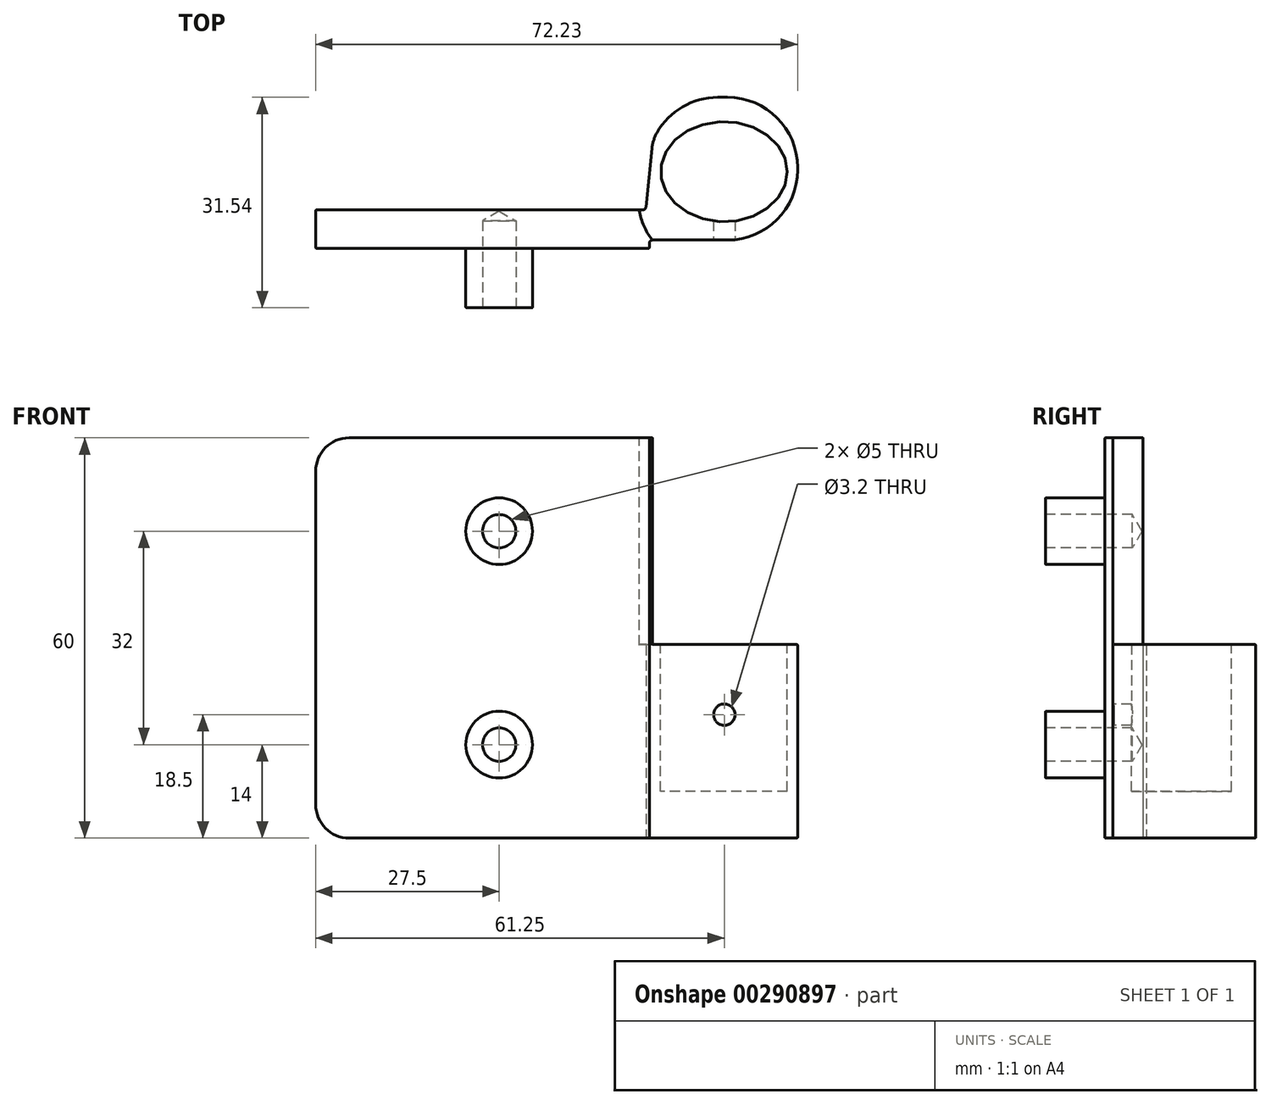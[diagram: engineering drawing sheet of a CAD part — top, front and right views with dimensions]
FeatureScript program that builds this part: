
annotation { "Feature Type Name" : "Feature", "Feature Type Description" : "" }
export const myFeature = defineFeature(function(context is Context, id is Id, definition is map)
    precondition{}
    {
        {
            var Q0;
            Q0=qCreatedBy(makeId("Front.planeOp"),FACE);
            var sketch = newSketch(context, id + "F0", { "sketchPlane" : qUnion([Q0])});
            skLineSegment(sketch, "E0", {"start": v(0, 0) * mm, "end": v(-48.5, 0) * mm});
            skLineSegment(sketch, "E1", {"start": v(-48.5, 0) * mm, "end": v(-48.5, -5.75) * mm});
            skLineSegment(sketch, "E2", {"start": v(-48.5, -5.75) * mm, "end": v(1.5, -5.75) * mm});
            skLineSegment(sketch, "E3", {"start": v(1.5, -5.75) * mm, "end": v(1.5, -5) * mm});
            skLineSegment(sketch, "E4", {"start": v(2, -4.5) * mm, "end": v(3.23, -4.5) * mm});
            skLineSegment(sketch, "E5", {"start": v(3.23, -4.5) * mm, "end": v(13.23, -4.5) * mm});
            skLineSegment(sketch, "E6", {"start": v(23.73, 6) * mm, "end": v(23.73, 6.4) * mm});
            skLineSegment(sketch, "E7", {"start": v(13.23, 16.9) * mm, "end": v(11.78, 16.9) * mm});
            skLineSegment(sketch, "E8", {"start": v(0.5, 0) * mm, "end": v(0, 0) * mm});
            skArc(sketch, "E9.filletArc", {"start": v(13.23, -4.5) * mm, "mid": v(20.66, -1.43) * mm, "end": v(23.73, 6) * mm});
            skArc(sketch, "E10.filletArc", {"start": v(23.73, 6.4) * mm, "mid": v(20.66, 13.82) * mm, "end": v(13.23, 16.9) * mm});
            skArc(sketch, "E11.filletArc", {"start": v(11.78, 16.9) * mm, "mid": v(6.5, 15.47) * mm, "end": v(2.65, 11.6) * mm});
            skArc(sketch, "E12.filletArc", {"start": v(0.5, 0) * mm, "mid": v(0.85, 0.15) * mm, "end": v(1, 0.5) * mm});
            skPoint(sketch, "E13.visualSharp", {"position": v(1.5, -4.5) * mm});
            skArc(sketch, "E13.filletArc", {"start": v(2, -4.5) * mm, "mid": v(1.65, -4.66) * mm, "end": v(1.5, -5) * mm});
            skLineSegment(sketch, "E14", {"start": v(1, 0.5) * mm, "end": v(1.9, 9.23) * mm});
            skPoint(sketch, "E15.visualSharp", {"position": v(2, 10.22) * mm});
            skArc(sketch, "E15.filletArc", {"start": v(2.65, 11.6) * mm, "mid": v(2.15, 10.45) * mm, "end": v(1.9, 9.23) * mm});
            skSolve(sketch);
        }
        {
            var Q0;
            Q0=makeQuery(id+"F0.imprint","IMPRINT",FACE,{"disambiguationData":[TD([[makeQuery(id+"F0.imprint","IMPRINT",EDGE,{"derivedFrom":sQuery(id+"F0.wireOp",EDGE,"E0")}),1.0]])]});
            extrude(context, id + "F1", {"entities" : qUnion([Q0]), "depth" : 60 * mm});
        }
        {
            var Q0;
            Q0=makeQuery(id+"F1.opExtrude","CAP_EDGE",EDGE,{"disambiguationData":[OSD([sQuery(id+"F0.wireOp",EDGE,"E1")])],"isStart":false});
            var Q1;
            Q1=makeQuery(id+"F1.opExtrude","CAP_EDGE",EDGE,{"disambiguationData":[OSD([sQuery(id+"F0.wireOp",EDGE,"E1")])],"isStart":true});
            fillet(context, id + "F2", {"entities" : qUnion([Q0, Q1]), "radius" : 5 * mm, "tangentPropagation" : true, "allowEdgeOverflow" : false});
        }
        {
            var Q0;
            Q0=makeQuery(id+"F1.opExtrude","SWEPT_FACE",FACE,{"disambiguationData":[OSD([sQuery(id+"F0.wireOp",EDGE,"E4"),sQuery(id+"F0.wireOp",EDGE,"E5")])]});
            var sketch = newSketch(context, id + "F3", { "sketchPlane" : qUnion([Q0])});
            skLineSegment(sketch, "E16.bottom", {"start": v(2, 60) * mm, "end": v(31.94, 60) * mm});
            skLineSegment(sketch, "E16.top", {"start": v(2, 29) * mm, "end": v(31.94, 29) * mm});
            skLineSegment(sketch, "E16.left", {"start": v(2, 60) * mm, "end": v(2, 29) * mm});
            skLineSegment(sketch, "E16.right", {"start": v(31.94, 60) * mm, "end": v(31.94, 29) * mm});
            skSolve(sketch);
        }
        {
            var Q0;
            Q0=qSketchRegion(id+"F3",true);
            extrude(context, id + "F4", {"entities" : qUnion([Q0]), "operationType" : NewBodyOperationType.REMOVE, "endBound" : BoundingType.THROUGH_ALL, "oppositeDirection" : true, "depth" : 25 * mm});
        }
        {
            var Q0;
            Q0=makeQuery(id+"F1.opExtrude","CAP_FACE",FACE,{"disambiguationData":[OSD([sQuery(id+"F0.wireOp",EDGE,"E0"),sQuery(id+"F0.wireOp",EDGE,"E1"),sQuery(id+"F0.wireOp",EDGE,"E2"),sQuery(id+"F0.wireOp",EDGE,"E3"),sQuery(id+"F0.wireOp",EDGE,"E4"),sQuery(id+"F0.wireOp",EDGE,"E5"),sQuery(id+"F0.wireOp",EDGE,"E6"),sQuery(id+"F0.wireOp",EDGE,"E7"),sQuery(id+"F0.wireOp",EDGE,"GG9Xp7Lx-0V8L-KjhP-dehT-RjXL1Wiv3JEy"),sQuery(id+"F0.wireOp",EDGE,"E8"),sQuery(id+"F0.wireOp",EDGE,"E9.filletArc"),sQuery(id+"F0.wireOp",EDGE,"E10.filletArc"),sQuery(id+"F0.wireOp",EDGE,"E11.filletArc"),sQuery(id+"F0.wireOp",EDGE,"E12.filletArc"),sQuery(id+"F0.wireOp",EDGE,"E13.filletArc")])],"isStart":false});
            var sketch = newSketch(context, id + "F5", { "sketchPlane" : qUnion([Q0])});
            skArc(sketch, "E17", {"start": v(0, 0) * mm, "mid": v(0.68, -2.4) * mm, "end": v(2, -4.5) * mm});
            skLineSegment(sketch, "E18", {"start": v(2, -4.5) * mm, "end": v(4.6, -0.03) * mm});
            skLineSegment(sketch, "E19", {"start": v(4.6, -0.03) * mm, "end": v(2.71, 13.2) * mm});
            skLineSegment(sketch, "E20", {"start": v(2.71, 13.2) * mm, "end": v(-1.4, 7.63) * mm});
            skLineSegment(sketch, "E21", {"start": v(0, 0) * mm, "end": v(-1.4, 7.63) * mm});
            skSolve(sketch);
        }
        {
            var Q0;
            Q0=qSketchRegion(id+"F5",true);
            extrude(context, id + "F6", {"entities" : qUnion([Q0]), "operationType" : NewBodyOperationType.REMOVE, "oppositeDirection" : true, "depth" : 31 * mm});
        }
        {
            var Q0;
            Q0=makeQuery(id+"F1.opExtrude","SWEPT_BODY",BODY,{"disambiguationData":[OSD([sQuery(id+"F0.wireOp",EDGE,"E0"),sQuery(id+"F0.wireOp",EDGE,"E1"),sQuery(id+"F0.wireOp",EDGE,"E2"),sQuery(id+"F0.wireOp",EDGE,"E3"),sQuery(id+"F0.wireOp",EDGE,"E4"),sQuery(id+"F0.wireOp",EDGE,"E5"),sQuery(id+"F0.wireOp",EDGE,"E6"),sQuery(id+"F0.wireOp",EDGE,"E7"),sQuery(id+"F0.wireOp",EDGE,"GG9Xp7Lx-0V8L-KjhP-dehT-RjXL1Wiv3JEy"),sQuery(id+"F0.wireOp",EDGE,"E8"),sQuery(id+"F0.wireOp",EDGE,"E9.filletArc"),sQuery(id+"F0.wireOp",EDGE,"E10.filletArc"),sQuery(id+"F0.wireOp",EDGE,"E11.filletArc"),sQuery(id+"F0.wireOp",EDGE,"E12.filletArc"),sQuery(id+"F0.wireOp",EDGE,"E13.filletArc")])]});
            var Q1;
            Q1=makeQuery(id+"F1.opExtrude","CAP_EDGE",EDGE,{"disambiguationData":[OSD([sQuery(id+"F0.wireOp",EDGE,"E0"),sQuery(id+"F0.wireOp",EDGE,"E8")])],"isStart":true});
            transform(context, id + "F7", {"entities" : qUnion([Q0]), "transformType" : TransformType.ROTATION, "transformAxis" : qUnion([Q1]), "angle" : 90 * degree, "makeCopy" : false});
        }
        {
            var Q0;
            Q0=makeQuery(id+"F1.opExtrude","SWEPT_FACE",FACE,{"disambiguationData":[OSD([sQuery(id+"F0.wireOp",EDGE,"E2")])]});
            var sketch = newSketch(context, id + "F8", { "sketchPlane" : qUnion([Q0])});
            skCircle(sketch, "E22", {"center": v(-21, 46) * mm, "radius": 5 * mm});
            skCircle(sketch, "E23", {"center": v(-21, 14) * mm, "radius": 5 * mm});
            skSolve(sketch);
        }
        {
            var Q0;
            Q0=qSketchRegion(id+"F8",true);
            extrude(context, id + "F9", {"entities" : qUnion([Q0]), "operationType" : NewBodyOperationType.ADD, "depth" : 8.9 * mm});
        }
        {
            var Q0;
            Q0=makeQuery(id+"F9.opExtrude","CAP_FACE",FACE,{"disambiguationData":[OSD([sQuery(id+"F8.wireOp",EDGE,"E22")])],"isStart":false});
            var sketch = newSketch(context, id + "F10", { "sketchPlane" : qUnion([Q0])});
            skCircle(sketch, "E24", {"center": v(-21, 46) * mm, "radius": 2.5 * mm});
            skSolve(sketch);
        }
        {
            var Q0;
            Q0=makeQuery(id+"F9.opExtrude","CAP_FACE",FACE,{"disambiguationData":[OSD([sQuery(id+"F8.wireOp",EDGE,"E23")])],"isStart":false});
            var sketch = newSketch(context, id + "F11", { "sketchPlane" : qUnion([Q0])});
            skCircle(sketch, "E25", {"center": v(-21, 14) * mm, "radius": 2.5 * mm});
            skSolve(sketch);
        }
        {
            var Q0;
            Q0=sQuery(id+"F10.wireOp",VERTEX,"E24.center");
            var Q1;
            Q1=makeQuery(id+"F1.opExtrude","SWEPT_BODY",BODY,{"disambiguationData":[OSD([sQuery(id+"F0.wireOp",EDGE,"E0"),sQuery(id+"F0.wireOp",EDGE,"E1"),sQuery(id+"F0.wireOp",EDGE,"E2"),sQuery(id+"F0.wireOp",EDGE,"E3"),sQuery(id+"F0.wireOp",EDGE,"E4"),sQuery(id+"F0.wireOp",EDGE,"E5"),sQuery(id+"F0.wireOp",EDGE,"E6"),sQuery(id+"F0.wireOp",EDGE,"E7"),sQuery(id+"F0.wireOp",EDGE,"GG9Xp7Lx-0V8L-KjhP-dehT-RjXL1Wiv3JEy"),sQuery(id+"F0.wireOp",EDGE,"E8"),sQuery(id+"F0.wireOp",EDGE,"E9.filletArc"),sQuery(id+"F0.wireOp",EDGE,"E10.filletArc"),sQuery(id+"F0.wireOp",EDGE,"E11.filletArc"),sQuery(id+"F0.wireOp",EDGE,"E12.filletArc"),sQuery(id+"F0.wireOp",EDGE,"E13.filletArc")])]});
            hole(context, id + "F12", {"style" : HoleStyle.SIMPLE, "endStyle" : HoleEndStyle.BLIND, "standardTappedOrClearance" : lookupTablePath({ "standard" : "ISO", "engagement" : "75%", "pitch" : "1 mm", "size" : "M6", "type" : "Tapped" }), "standardBlindInLast" : lookupTablePath({ "standard" : "ISO", "engagement" : "75%", "pitch" : "1 mm", "size" : "M6", "type" : "Tapped" }), "holeDiameter" : 5 * mm, "showTappedDepth" : true, "holeDepth" : 13 * mm, "tappedDepth" : 10 * mm, "tapClearance" : 3, "locations" : qUnion([Q0]), "scope" : qUnion([Q1]), "majorDiameter" : 6 * mm});
        }
        {
            var Q0;
            Q0=sQuery(id+"F11.wireOp",VERTEX,"E25.center");
            var Q1;
            Q1=makeQuery(id+"F1.opExtrude","SWEPT_BODY",BODY,{"disambiguationData":[OSD([sQuery(id+"F0.wireOp",EDGE,"E0"),sQuery(id+"F0.wireOp",EDGE,"E1"),sQuery(id+"F0.wireOp",EDGE,"E2"),sQuery(id+"F0.wireOp",EDGE,"E3"),sQuery(id+"F0.wireOp",EDGE,"E4"),sQuery(id+"F0.wireOp",EDGE,"E5"),sQuery(id+"F0.wireOp",EDGE,"E6"),sQuery(id+"F0.wireOp",EDGE,"E7"),sQuery(id+"F0.wireOp",EDGE,"GG9Xp7Lx-0V8L-KjhP-dehT-RjXL1Wiv3JEy"),sQuery(id+"F0.wireOp",EDGE,"E8"),sQuery(id+"F0.wireOp",EDGE,"E9.filletArc"),sQuery(id+"F0.wireOp",EDGE,"E10.filletArc"),sQuery(id+"F0.wireOp",EDGE,"E11.filletArc"),sQuery(id+"F0.wireOp",EDGE,"E12.filletArc"),sQuery(id+"F0.wireOp",EDGE,"E13.filletArc")])]});
            hole(context, id + "F13", {"style" : HoleStyle.SIMPLE, "endStyle" : HoleEndStyle.BLIND, "standardTappedOrClearance" : lookupTablePath({ "standard" : "ISO", "engagement" : "75%", "pitch" : "1 mm", "size" : "M6", "type" : "Tapped" }), "standardBlindInLast" : lookupTablePath({ "standard" : "ISO", "engagement" : "75%", "pitch" : "1 mm", "size" : "M6", "type" : "Tapped" }), "holeDiameter" : 5 * mm, "showTappedDepth" : true, "holeDepth" : 13 * mm, "tappedDepth" : 10 * mm, "tapClearance" : 3, "locations" : qUnion([Q0]), "scope" : qUnion([Q1]), "majorDiameter" : 6 * mm});
        }
        {
            var Q0;
            Q0=makeQuery(id+"F6.boolean.opBoolean","MERGE",FACE,{"derivedFrom":[makeQuery(id+"F4.boolean.opBoolean","COPY",FACE,{"derivedFrom":makeQuery(id+"F4.opExtrude","SWEPT_FACE",FACE,{"disambiguationData":[OSD([sQuery(id+"F3.wireOp",EDGE,"E16.top")])]})}),makeQuery(id+"F6.opExtrude","CAP_FACE",FACE,{"disambiguationData":[OSD([sQuery(id+"F5.wireOp",EDGE,"E17"),sQuery(id+"F5.wireOp",EDGE,"E18"),sQuery(id+"F5.wireOp",EDGE,"E19"),sQuery(id+"F5.wireOp",EDGE,"E20"),sQuery(id+"F5.wireOp",EDGE,"E21")])],"isStart":false})]});
            var sketch = newSketch(context, id + "F14", { "sketchPlane" : qUnion([Q0])});
            skEllipse(sketch, "E26", {"center": v(12.7, 5.75) * mm, "majorRadius": 9.5 * mm, "minorRadius": 7.5 * mm, "majorAxis": v(1, 0)});
            skSolve(sketch);
        }
        {
            var Q0;
            Q0=qSketchRegion(id+"F14",true);
            extrude(context, id + "F15", {"entities" : qUnion([Q0]), "operationType" : NewBodyOperationType.REMOVE, "oppositeDirection" : true, "depth" : 22 * mm});
        }
        {
            var Q0;
            Q0=makeQuery(id+"F1.opExtrude","SWEPT_FACE",FACE,{"disambiguationData":[OSD([sQuery(id+"F0.wireOp",EDGE,"E4"),sQuery(id+"F0.wireOp",EDGE,"E5")])]});
            var sketch = newSketch(context, id + "F16", { "sketchPlane" : qUnion([Q0])});
            skCircle(sketch, "E27", {"center": v(12.75, 18.5) * mm, "radius": 1.5 * mm});
            skSolve(sketch);
        }
        {
            var Q0;
            Q0=sQuery(id+"F16.wireOp",VERTEX,"E27.center");
            var Q1;
            Q1=makeQuery(id+"F1.opExtrude","SWEPT_BODY",BODY,{"disambiguationData":[OSD([sQuery(id+"F0.wireOp",EDGE,"E0"),sQuery(id+"F0.wireOp",EDGE,"E1"),sQuery(id+"F0.wireOp",EDGE,"E2"),sQuery(id+"F0.wireOp",EDGE,"E3"),sQuery(id+"F0.wireOp",EDGE,"E4"),sQuery(id+"F0.wireOp",EDGE,"E5"),sQuery(id+"F0.wireOp",EDGE,"E6"),sQuery(id+"F0.wireOp",EDGE,"E7"),sQuery(id+"F0.wireOp",EDGE,"E8"),sQuery(id+"F0.wireOp",EDGE,"E9.filletArc"),sQuery(id+"F0.wireOp",EDGE,"E10.filletArc"),sQuery(id+"F0.wireOp",EDGE,"E11.filletArc"),sQuery(id+"F0.wireOp",EDGE,"E12.filletArc"),sQuery(id+"F0.wireOp",EDGE,"E13.filletArc"),sQuery(id+"F0.wireOp",EDGE,"E14"),sQuery(id+"F0.wireOp",EDGE,"E15.filletArc")])]});
            hole(context, id + "F17", {"style" : HoleStyle.SIMPLE, "endStyle" : HoleEndStyle.BLIND, "standardTappedOrClearance" : lookupTablePath({ "standard" : "ISO", "engagement" : "75%", "pitch" : "0.75 mm", "size" : "M4", "type" : "Tapped" }), "standardBlindInLast" : lookupTablePath({ "standard" : "ISO", "engagement" : "75%", "pitch" : "0.75 mm", "size" : "M4", "type" : "Tapped" }), "holeDiameter" : 3.2 * mm, "showTappedDepth" : true, "holeDepth" : 12.25 * mm, "tappedDepth" : 10 * mm, "tapClearance" : 3, "locations" : qUnion([Q0]), "scope" : qUnion([Q1])});
        }
        {
            var Q0;
            Q0=makeQuery(id+"F15.boolean.opBoolean","COPY",EDGE,{"derivedFrom":makeQuery(id+"F15.opExtrude","CAP_EDGE",EDGE,{"disambiguationData":[OSD([sQuery(id+"F14.wireOp",EDGE,"E26")])],"isStart":true})});
            var Q1;
            Q1=makeQuery(id+"F6.boolean.opBoolean","INTERSECT",EDGE,{"derivedFrom":[makeQuery(id+"F1.opExtrude","SWEPT_FACE",FACE,{"disambiguationData":[OSD([sQuery(id+"F0.wireOp",EDGE,"E12.filletArc")])]}),makeQuery(id+"F6.opExtrude","CAP_FACE",FACE,{"disambiguationData":[OSD([sQuery(id+"F5.wireOp",EDGE,"E17"),sQuery(id+"F5.wireOp",EDGE,"E18"),sQuery(id+"F5.wireOp",EDGE,"E19"),sQuery(id+"F5.wireOp",EDGE,"E20"),sQuery(id+"F5.wireOp",EDGE,"E21")])],"isStart":false})]});
            var Q2;
            Q2=makeQuery(id+"F6.boolean.opBoolean","INTERSECT",EDGE,{"derivedFrom":[makeQuery(id+"F1.opExtrude","SWEPT_FACE",FACE,{"disambiguationData":[OSD([sQuery(id+"F0.wireOp",EDGE,"E14")])]}),makeQuery(id+"F6.opExtrude","CAP_FACE",FACE,{"disambiguationData":[OSD([sQuery(id+"F5.wireOp",EDGE,"E17"),sQuery(id+"F5.wireOp",EDGE,"E18"),sQuery(id+"F5.wireOp",EDGE,"E19"),sQuery(id+"F5.wireOp",EDGE,"E20"),sQuery(id+"F5.wireOp",EDGE,"E21")])],"isStart":false})]});
            var Q3;
            Q3=makeQuery(id+"F1.opExtrude","CAP_EDGE",EDGE,{"disambiguationData":[OSD([sQuery(id+"F0.wireOp",EDGE,"E0"),sQuery(id+"F0.wireOp",EDGE,"E8")])],"isStart":false});
            var Q4;
            Q4=makeQuery(id+"F1.opExtrude","CAP_EDGE",EDGE,{"disambiguationData":[OSD([sQuery(id+"F0.wireOp",EDGE,"E2")])],"isStart":false});
            var Q5;
            Q5=makeQuery(id+"F1.opExtrude","CAP_EDGE",EDGE,{"disambiguationData":[OSD([sQuery(id+"F0.wireOp",EDGE,"E14")])],"isStart":true});
            var Q6;
            Q6=makeQuery(id+"F1.opExtrude","SWEPT_EDGE",EDGE,{"disambiguationData":[OSD([sQuery(id+"F0.wireOp",EDGE,"E2"),sQuery(id+"F0.wireOp",EDGE,"E3")])]});
            var Q7;
            Q7=makeQuery(id+"F6.boolean.opBoolean","COPY",EDGE,{"derivedFrom":makeQuery(id+"F6.opExtrude","SWEPT_EDGE",EDGE,{"disambiguationData":[OSD([sQuery(id+"F0.wireOp",EDGE,"E0"),sQuery(id+"F0.wireOp",EDGE,"E8"),sQuery(id+"F5.wireOp",EDGE,"E17"),sQuery(id+"F5.wireOp",EDGE,"E21")])]})});
            var Q8;
            Q8=makeQuery(id+"F6.boolean.opBoolean","COPY",EDGE,{"derivedFrom":makeQuery(id+"F6.opExtrude","CAP_EDGE",EDGE,{"disambiguationData":[OSD([sQuery(id+"F5.wireOp",EDGE,"E17")])],"isStart":true})});
            var Q9;
            Q9=makeQuery(id+"F1.opExtrude","CAP_EDGE",EDGE,{"disambiguationData":[OSD([sQuery(id+"F0.wireOp",EDGE,"E13.filletArc")])],"isStart":false});
            var Q10;
            Q10=makeQuery(id+"F9.opExtrude","CAP_EDGE",EDGE,{"disambiguationData":[OSD([sQuery(id+"F8.wireOp",EDGE,"E22")])],"isStart":false});
            var Q11;
            Q11=makeQuery(id+"F9.opExtrude","CAP_EDGE",EDGE,{"disambiguationData":[OSD([sQuery(id+"F8.wireOp",EDGE,"E23")])],"isStart":false});
            var Q12;
            Q12=makeQuery(id+"F9.opExtrude","CAP_EDGE",EDGE,{"disambiguationData":[OSD([sQuery(id+"F8.wireOp",EDGE,"E22")])],"isStart":true});
            var Q13;
            Q13=makeQuery(id+"F9.opExtrude","CAP_EDGE",EDGE,{"disambiguationData":[OSD([sQuery(id+"F8.wireOp",EDGE,"E23")])],"isStart":true});
            fillet(context, id + "F18", {"entities" : qUnion([Q0, Q1, Q2, Q3, Q4, Q5, Q6, Q7, Q8, Q9, Q10, Q11, Q12, Q13]), "radius" : 0.1 * mm, "tangentPropagation" : true, "allowEdgeOverflow" : false});
        }
    });
